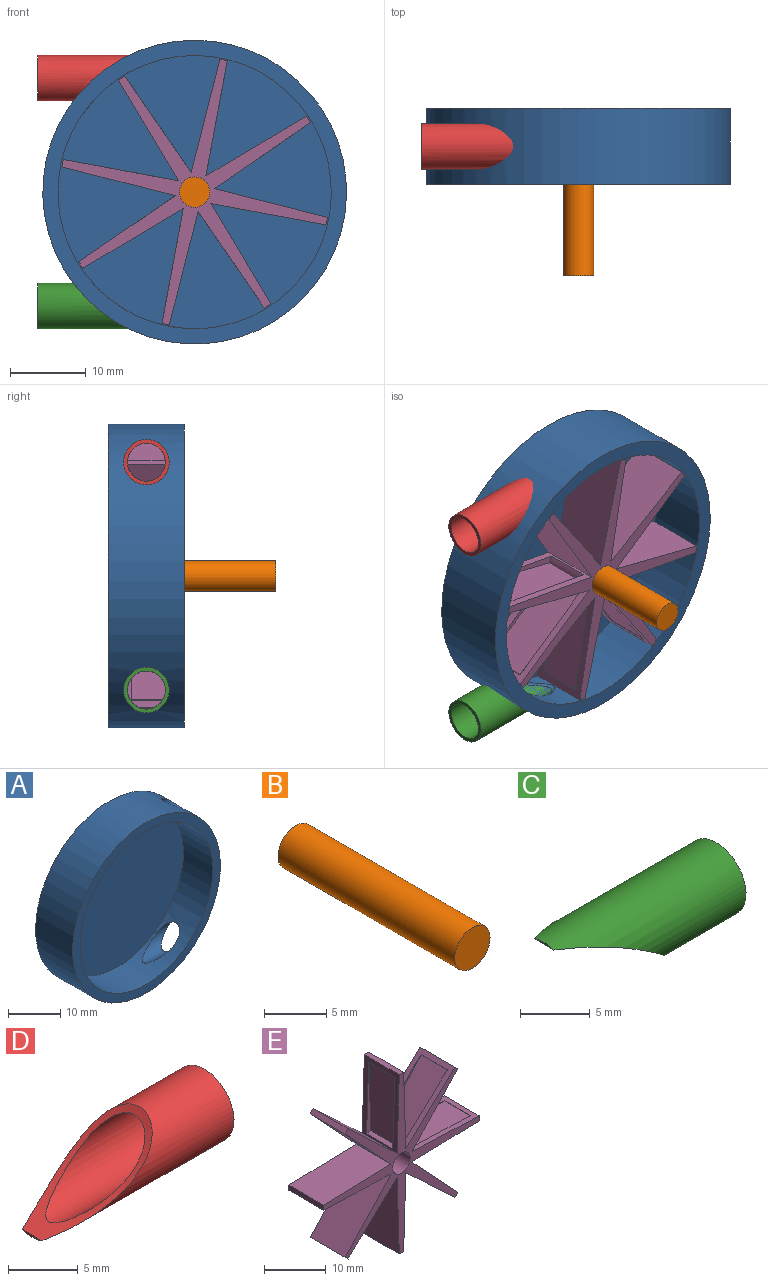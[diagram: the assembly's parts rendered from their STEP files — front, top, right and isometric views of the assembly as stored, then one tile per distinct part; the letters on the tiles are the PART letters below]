
ASSEMBLY  parts=5 mates=4
PART A: 7 faces, bbox 40x10x40 mm
  f0: cylinder r=20mm len=40mm, axis (0,1,0), area 1195.8mm2, adj f2,f3,f5,f6
  f1: cylinder r=18mm len=36mm, axis (0,1,0), area 828.7mm2, adj f2,f4,f5,f6
  f2: plane 40x40mm, normal (0,-1,0), area 238.8mm2, adj f0,f1
  f3: plane 40x40mm, normal (0,1,0), area 1256.6mm2, adj f0
  f4: plane 36x36mm, normal (0,-1,0), area 1017.9mm2, adj f1
  f5: cylinder r=2.5mm len=11.4mm, axis (1,0,0), area 56.9mm2, adj f0,f1
  f6: cylinder r=2.5mm len=11.4mm, axis (1,0,0), area 56.9mm2, adj f0,f1
PART B: 3 faces, bbox 4x20x4 mm
  f0: cylinder r=2mm len=20mm, axis (0,1,0), area 251.3mm2, adj f1,f2
  f1: plane 4x4mm, normal (0,-1,0), area 12.6mm2, adj f0
  f2: plane 4x4mm, normal (0,1,0), area 12.6mm2, adj f0
PART C: 5 faces, bbox 17.5x6x6 mm
  f0: cylinder r=3mm len=17.49mm, axis (1,0,0), area 208.2mm2, adj f1,f2,f3
  f1: plane 2.02x0.18mm, normal (-1,0,0), area 0.2mm2, adj f0,f3
  f2: plane 6x6mm, normal (1,0,0), area 8.6mm2, adj f0,f4
  f3: cylinder r=18mm len=10.91mm, axis (0,1,0), area 19.7mm2, adj f0,f1,f4
  f4: cylinder r=2.5mm len=15.79mm, axis (1,0,0), area 167.7mm2, adj f2,f3
PART D: 5 faces, bbox 17.5x6x6 mm
  f0: cylinder r=3mm len=17.49mm, axis (1,0,0), area 208.2mm2, adj f1,f2,f3
  f1: plane 2.02x0.18mm, normal (-1,0,0), area 0.2mm2, adj f0,f3
  f2: plane 6x6mm, normal (1,0,0), area 8.6mm2, adj f0,f4
  f3: cylinder r=18mm len=10.91mm, axis (0,1,0), area 19.7mm2, adj f0,f1,f4
  f4: cylinder r=2.5mm len=15.79mm, axis (1,0,0), area 167.8mm2, adj f2,f3
PART E: 67 faces, bbox 35.6x8x35.6 mm
  f0: plane 15.39x8mm, normal (1,0,-0.03), area 39.4mm2, adj f8,f23,f24,f25,f62,f63,f65,f66
  f1: plane 11.24x10.53mm, normal (0.68,0,-0.73), area 39.4mm2, adj f21,f22,f24,f25,f57,f58,f60,f61
  f2: plane 15.39x8mm, normal (-0.03,0,-1), area 39.4mm2, adj f19,f20,f24,f25,f52,f54,f55,f56
  f3: plane 11.24x10.53mm, normal (-0.73,0,-0.68), area 39.4mm2, adj f17,f18,f24,f25,f47,f49,f50,f51
  f4: plane 15.39x8mm, normal (-1,0,0.03), area 39.4mm2, adj f15,f16,f24,f25,f42,f44,f45,f46
  f5: plane 11.24x10.53mm, normal (-0.68,0,0.73), area 39.4mm2, adj f13,f14,f24,f25,f37,f39,f40,f41
  f6: plane 15.39x8mm, normal (0.03,0,1), area 39.4mm2, adj f11,f12,f24,f25,f32,f34,f35,f36
  f7: plane 11.24x10.53mm, normal (0.73,0,0.68), area 39.4mm2, adj f9,f10,f24,f25,f27,f28,f30,f31
  f8: plane 11.24x10.53mm, normal (-0.68,0,-0.73), area 123.2mm2, adj f0,f9,f24,f25
  f9: plane 8x0.71mm, normal (0.71,0,-0.71), area 8mm2, adj f7,f8,f24,f25
  f10: plane 15.39x8mm, normal (0.03,0,-1), area 123.2mm2, adj f7,f11,f24,f25
  f11: plane 8x1mm, normal (1,0,0), area 8mm2, adj f6,f10,f24,f25
  f12: plane 11.24x10.53mm, normal (0.73,0,-0.68), area 123.2mm2, adj f6,f13,f24,f25
  f13: plane 8x0.71mm, normal (0.71,0,0.71), area 8mm2, adj f5,f12,f24,f25
  f14: plane 15.39x8mm, normal (1,0,0.03), area 123.2mm2, adj f5,f15,f24,f25
  f15: plane 8x1mm, normal (0,0,1), area 8mm2, adj f4,f14,f24,f25
  f16: plane 11.24x10.53mm, normal (0.68,0,0.73), area 123.2mm2, adj f4,f17,f24,f25
  f17: plane 8x0.71mm, normal (-0.71,0,0.71), area 8mm2, adj f3,f16,f24,f25
  f18: plane 15.39x8mm, normal (-0.03,0,1), area 123.2mm2, adj f3,f19,f24,f25
  f19: plane 8x1mm, normal (-1,0,0), area 8mm2, adj f2,f18,f24,f25
  f20: plane 11.24x10.53mm, normal (-0.73,0,0.68), area 123.2mm2, adj f2,f21,f24,f25
  f21: plane 8x0.71mm, normal (-0.71,0,-0.71), area 8mm2, adj f1,f20,f24,f25
  f22: plane 15.39x8mm, normal (-1,0,-0.03), area 123.2mm2, adj f1,f23,f24,f25
  f23: plane 8x1mm, normal (0,0,-1), area 8mm2, adj f0,f22,f24,f25
  f24: plane 35.6x35.6mm, normal (0,-1,0), area 190.9mm2, adj f0,f1,f2,f3,f4,f5,f6,f7
  f25: plane 35.6x35.6mm, normal (0,1,0), area 190.9mm2, adj f0,f1,f2,f3,f4,f5,f6,f7
  f26: cylinder r=2mm len=8mm, axis (0,-1,0), area 100.5mm2, adj f24,f25
  f27: plane 10.24x10.12mm, normal (0,-1,0), area 7.1mm2, adj f7,f28,f29,f31
  f28: plane 6x0.05mm, normal (-0.71,0,0.71), area 0.4mm2, adj f7,f27,f29,f30
  f29: plane 10.07x9.44mm, normal (0.68,0,0.73), area 82.8mm2, adj f27,f28,f30,f31
  f30: plane 10.24x10.12mm, normal (0,1,0), area 7.1mm2, adj f7,f28,f29,f31
  f31: cylinder r=3mm len=6mm, axis (0,-1,0), area 5.9mm2, adj f7,f27,f29,f30
  f32: plane 6x0.06mm, normal (-1,0,0), area 0.4mm2, adj f6,f33,f34,f35
  f33: plane 13.8x6mm, normal (-0.03,0,1), area 82.8mm2, adj f32,f34,f35,f36
  f34: plane 13.97x0.96mm, normal (0,1,0), area 7.1mm2, adj f6,f32,f33,f36
  f35: plane 13.97x0.96mm, normal (0,-1,0), area 7.1mm2, adj f6,f32,f33,f36
  f36: cylinder r=3mm len=6mm, axis (0,-1,0), area 5.9mm2, adj f6,f33,f34,f35
  f37: plane 6x0.05mm, normal (-0.71,0,-0.71), area 0.4mm2, adj f5,f38,f39,f40
  f38: plane 10.07x9.44mm, normal (-0.73,0,0.68), area 82.8mm2, adj f37,f39,f40,f41
  f39: plane 10.24x10.12mm, normal (0,1,0), area 7.1mm2, adj f5,f37,f38,f41
  f40: plane 10.24x10.12mm, normal (0,-1,0), area 7.1mm2, adj f5,f37,f38,f41
  f41: cylinder r=3mm len=6mm, axis (0,-1,0), area 5.9mm2, adj f5,f38,f39,f40
  f42: plane 6x0.06mm, normal (0,0,-1), area 0.4mm2, adj f4,f43,f44,f45
  f43: plane 13.8x6mm, normal (-1,0,-0.03), area 82.8mm2, adj f42,f44,f45,f46
  f44: plane 13.97x0.96mm, normal (0,1,0), area 7.1mm2, adj f4,f42,f43,f46
  f45: plane 13.97x0.96mm, normal (0,-1,0), area 7.1mm2, adj f4,f42,f43,f46
  f46: cylinder r=3mm len=6mm, axis (0,-1,0), area 5.9mm2, adj f4,f43,f44,f45
  f47: plane 6x0.05mm, normal (0.71,0,-0.71), area 0.4mm2, adj f3,f48,f49,f50
  f48: plane 10.07x9.44mm, normal (-0.68,0,-0.73), area 82.8mm2, adj f47,f49,f50,f51
  f49: plane 10.24x10.12mm, normal (0,1,0), area 7.1mm2, adj f3,f47,f48,f51
  f50: plane 10.24x10.12mm, normal (0,-1,0), area 7.1mm2, adj f3,f47,f48,f51
  f51: cylinder r=3mm len=6mm, axis (0,-1,0), area 5.9mm2, adj f3,f48,f49,f50
  f52: plane 6x0.06mm, normal (1,0,0), area 0.4mm2, adj f2,f53,f54,f55
  f53: plane 13.8x6mm, normal (0.03,0,-1), area 82.8mm2, adj f52,f54,f55,f56
  f54: plane 13.97x0.96mm, normal (0,1,0), area 7.1mm2, adj f2,f52,f53,f56
  f55: plane 13.97x0.96mm, normal (0,-1,0), area 7.1mm2, adj f2,f52,f53,f56
  f56: cylinder r=3mm len=6mm, axis (0,-1,0), area 5.9mm2, adj f2,f53,f54,f55
  f57: plane 10.24x10.12mm, normal (0,1,0), area 7.1mm2, adj f1,f58,f59,f61
  f58: plane 6x0.05mm, normal (0.71,0,0.71), area 0.4mm2, adj f1,f57,f59,f60
  f59: plane 10.07x9.44mm, normal (0.73,0,-0.68), area 82.8mm2, adj f57,f58,f60,f61
  f60: plane 10.24x10.12mm, normal (0,-1,0), area 7.1mm2, adj f1,f58,f59,f61
  f61: cylinder r=3mm len=6mm, axis (0,-1,0), area 5.9mm2, adj f1,f57,f59,f60
  f62: plane 13.97x0.96mm, normal (0,-1,0), area 7.1mm2, adj f0,f64,f65,f66
  f63: plane 13.97x0.96mm, normal (0,1,0), area 7.1mm2, adj f0,f64,f65,f66
  f64: plane 13.8x6mm, normal (1,0,0.03), area 82.8mm2, adj f62,f63,f65,f66
  f65: plane 6x0.06mm, normal (0,0,1), area 0.4mm2, adj f0,f62,f63,f64
  f66: cylinder r=3mm len=6mm, axis (0,-1,0), area 5.9mm2, adj f0,f62,f63,f64
PLACE A rot(axis=(0,1,0),180deg) t=(-19.27,11.84,3.3)mm fixed
PLACE B rot(axis=(1,0,0),180deg) t=(-19.27,-5.16,3.3)mm
PLACE C rot(axis=(0,1,0),180deg) t=(-19.95,11.84,3.3)mm
PLACE D rot(axis=(0,1,0),180deg) t=(-19.95,11.84,3.3)mm
PLACE E rot(axis=(0.78,0,0.63),180deg) t=(-19.27,10.84,3.3)mm
MATE fastened B.f0 <-> A.f0  axis (0,1,0) through (-19.27,14.84,3.3)mm
MATE fastened C.f0 <-> A.f6  axis (-1,0,0) through (-39.95,11.84,-11.7)mm
MATE fastened D.f0 <-> A.f5  axis (-1,0,0) through (-39.95,11.84,18.3)mm
MATE revolute E.f26 <-> B.f0  axis (0,1,0) through (-19.27,14.84,3.3)mm
